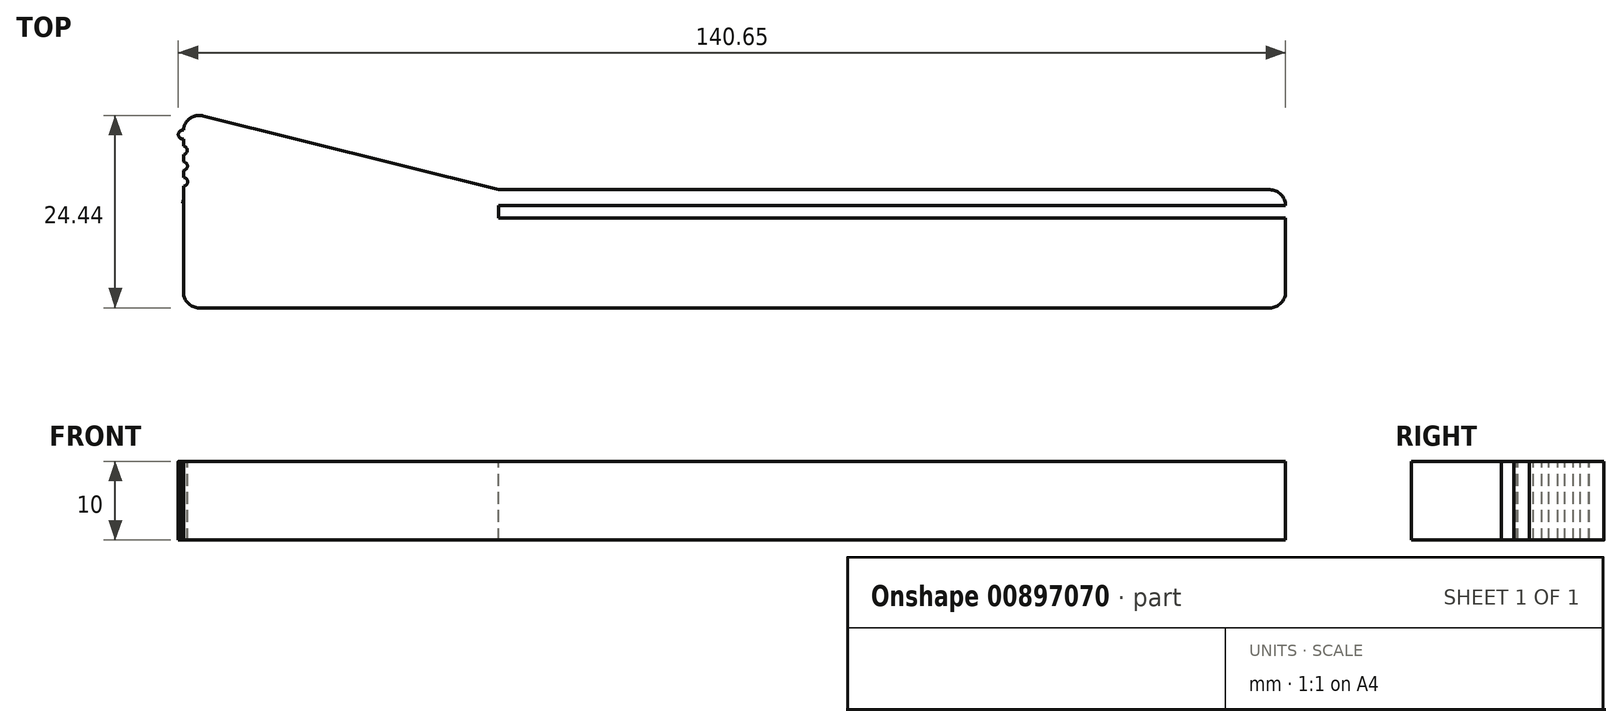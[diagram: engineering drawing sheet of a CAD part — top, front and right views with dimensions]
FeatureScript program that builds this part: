
annotation { "Feature Type Name" : "Feature", "Feature Type Description" : "" }
export const myFeature = defineFeature(function(context is Context, id is Id, definition is map)
    precondition{}
    {
        {
            var Q0;
            Q0=qCreatedBy(makeId("Top.planeOp"),FACE);
            var sketch = newSketch(context, id + "F0", { "sketchPlane" : qUnion([Q0])});
            skLineSegment(sketch, "E0.bottom", {"start": v(0, 7.5) * mm, "end": v(98, 7.5) * mm});
            skLineSegment(sketch, "E0.top", {"start": v(0, -7.5) * mm, "end": v(98, -7.5) * mm});
            skLineSegment(sketch, "E0.left", {"start": v(0, 7.5) * mm, "end": v(0, -7.5) * mm});
            skLineSegment(sketch, "E0.right", {"start": v(100, 5.5) * mm, "end": v(100, -5.5) * mm});
            skLineSegment(sketch, "E1", {"start": v(0, -7.5) * mm, "end": v(-38, -7.5) * mm});
            skLineSegment(sketch, "E2", {"start": v(-40, -5.5) * mm, "end": v(-40, 14.94) * mm});
            skLineSegment(sketch, "E3", {"start": v(-37.51, 16.88) * mm, "end": v(0, 7.5) * mm});
            skPoint(sketch, "E4.visualSharp", {"position": v(-40, 17.5) * mm});
            skArc(sketch, "E4.filletArc", {"start": v(-37.51, 16.88) * mm, "mid": v(-39.23, 16.51) * mm, "end": v(-40, 14.94) * mm});
            skPoint(sketch, "E5.visualSharp", {"position": v(-40, -7.5) * mm});
            skArc(sketch, "E5.filletArc", {"start": v(-40, -5.5) * mm, "mid": v(-39.41, -6.91) * mm, "end": v(-38, -7.5) * mm});
            skPoint(sketch, "E6.visualSharp", {"position": v(100, 7.5) * mm});
            skArc(sketch, "E6.filletArc", {"start": v(100, 5.5) * mm, "mid": v(99.41, 6.91) * mm, "end": v(98, 7.5) * mm});
            skPoint(sketch, "E7.visualSharp", {"position": v(100, -7.5) * mm});
            skArc(sketch, "E7.filletArc", {"start": v(98, -7.5) * mm, "mid": v(99.41, -6.91) * mm, "end": v(100, -5.5) * mm});
            skPoint(sketch, "E8", {"position": v(-14, -1.5) * mm});
            skLineSegment(sketch, "E9.bottom", {"start": v(-18.83, -0.2) * mm, "end": v(-43.6, -0.2) * mm});
            skLineSegment(sketch, "E9.top", {"start": v(-18.83, -2.8) * mm, "end": v(-43.6, -2.8) * mm});
            skLineSegment(sketch, "E9.left", {"start": v(-18.83, -0.2) * mm, "end": v(-18.83, -2.8) * mm});
            skLineSegment(sketch, "E9.right", {"start": v(-43.6, -0.2) * mm, "end": v(-43.6, -2.8) * mm});
            skCircle(sketch, "E10", {"center": v(-14, -1.5) * mm, "radius": 5 * mm});
            skLineSegment(sketch, "E11", {"start": v(-15.93, 3.11) * mm, "end": v(-23.83, -0.2) * mm});
            skLineSegment(sketch, "E12", {"start": v(-15.93, -6.11) * mm, "end": v(-23.83, -2.8) * mm});
            skCircle(sketch, "E13", {"center": v(-14, -1.5) * mm, "radius": 3.4 * mm});
            skLineSegment(sketch, "E14.bottom", {"start": v(100, 5.5) * mm, "end": v(-40, 5.5) * mm});
            skLineSegment(sketch, "E14.top", {"start": v(100, 3.9) * mm, "end": v(-40, 3.9) * mm});
            skLineSegment(sketch, "E14.left", {"start": v(100, 5.5) * mm, "end": v(100, 3.9) * mm});
            skLineSegment(sketch, "E14.right", {"start": v(-40, 5.5) * mm, "end": v(-40, 3.9) * mm});
            skCircle(sketch, "E15", {"center": v(-40, 6.51) * mm, "radius": 0.56 * mm});
            skCircle(sketch, "E16.1.0.0", {"center": v(-40.02, 8.51) * mm, "radius": 0.56 * mm});
            skCircle(sketch, "E16.2.0.0", {"center": v(-40.05, 10.5) * mm, "radius": 0.56 * mm});
            skCircle(sketch, "E16.3.0.0", {"center": v(-40.07, 12.5) * mm, "radius": 0.56 * mm});
            skCircle(sketch, "E16.4.0.0", {"center": v(-40.1, 14.5) * mm, "radius": 0.56 * mm});
            skLineSegment(sketch, "E16.direction1", {"start": v(-40, 6.51) * mm, "end": v(-40.02, 8.51) * mm, "construction": true});
            skLineSegment(sketch, "E17", {"start": v(-40.26, 6.02) * mm, "end": v(-39.23, 5.5) * mm});
            skLineSegment(sketch, "E18", {"start": v(-15.32, 1.64) * mm, "end": v(-22.8, -1.5) * mm});
            skLineSegment(sketch, "E19", {"start": v(-22.8, -1.5) * mm, "end": v(-15.32, -4.64) * mm});
            skSolve(sketch);
        }
        {
            var Q0;
            Q0=makeQuery(id+"F0.imprint","IMPRINT",FACE,{"disambiguationData":[TD([[makeQuery(id+"F0.imprint","IMPRINT",EDGE,{"derivedFrom":sQuery(id+"F0.wireOp",EDGE,"E0.left")}),-1.0]])]});
            var Q1;
            Q1=makeQuery(id+"F0.imprint","IMPRINT",FACE,{"disambiguationData":[TD([[makeQuery(id+"F0.imprint","IMPRINT",EDGE,{"derivedFrom":sQuery(id+"F0.wireOp",EDGE,"E0.bottom")}),-1.0]])]});
            var Q2;
            {var subQ5=sQuery(id+"F0.wireOp",EDGE,"E9.left");Q2=makeQuery(id+"F0.imprint","IMPRINT",FACE,{"disambiguationData":[TD([[makeQuery(id+"F0.imprint","IMPRINT",EDGE,{"derivedFrom":subQ5}),-1.0]])]});}
            var Q3;
            Q3=makeQuery(id+"F0.imprint","IMPRINT",FACE,{"disambiguationData":[TD([[makeQuery(id+"F0.imprint","IMPRINT",EDGE,{"derivedFrom":sQuery(id+"F0.wireOp",EDGE,"E13")}),1.0]])]});
            var Q4;
            {var subQ2=sQuery(id+"F0.wireOp",EDGE,"E2");var subQ7=sQuery(id+"F0.wireOp",EDGE,"E9.top");var subQ10=makeQuery(id+"F0.imprint","INTERSECT",VERTEX,{"derivedFrom":[subQ2,subQ7]});Q4=makeQuery(id+"F0.imprint","IMPRINT",FACE,{"disambiguationData":[TD([[makeQuery(id+"F0.imprint","IMPRINT",EDGE,{"disambiguationData":[TD([[subQ10,-1.0]])],"derivedFrom":subQ2}),-1.0]])]});}
            var Q5;
            {var subQ3=sQuery(id+"F0.wireOp",EDGE,"E12");Q5=makeQuery(id+"F0.imprint","IMPRINT",FACE,{"disambiguationData":[TD([[makeQuery(id+"F0.imprint","IMPRINT",EDGE,{"derivedFrom":subQ3}),-1.0]])]});}
            var Q6;
            {var subQ3=sQuery(id+"F0.wireOp",EDGE,"E11");Q6=makeQuery(id+"F0.imprint","IMPRINT",FACE,{"disambiguationData":[TD([[makeQuery(id+"F0.imprint","IMPRINT",EDGE,{"derivedFrom":subQ3}),1.0]])]});}
            var Q7;
            {var subQ1=sQuery(id+"F0.wireOp",EDGE,"E9.left");Q7=makeQuery(id+"F0.imprint","IMPRINT",FACE,{"disambiguationData":[TD([[makeQuery(id+"F0.imprint","IMPRINT",EDGE,{"derivedFrom":subQ1}),1.0]])]});}
            var Q8;
            {var subQ0=sQuery(id+"F0.wireOp",EDGE,"E3");Q8=makeQuery(id+"F0.imprint","IMPRINT",FACE,{"disambiguationData":[TD([[makeQuery(id+"F0.imprint","IMPRINT",EDGE,{"derivedFrom":subQ0}),-1.0]])]});}
            var Q9;
            {var subQ3=sQuery(id+"F0.wireOp",EDGE,"E1");Q9=makeQuery(id+"F0.imprint","IMPRINT",FACE,{"disambiguationData":[TD([[makeQuery(id+"F0.imprint","IMPRINT",EDGE,{"derivedFrom":subQ3}),-1.0]])]});}
            var Q10;
            {var subQ1=sQuery(id+"F0.wireOp",EDGE,"E0.top");Q10=makeQuery(id+"F0.imprint","IMPRINT",FACE,{"disambiguationData":[TD([[makeQuery(id+"F0.imprint","IMPRINT",EDGE,{"derivedFrom":subQ1}),1.0]])]});}
            var Q11;
            {var subQ5=sQuery(id+"F0.wireOp",EDGE,"E14.left");Q11=makeQuery(id+"F0.imprint","IMPRINT",FACE,{"disambiguationData":[TD([[makeQuery(id+"F0.imprint","IMPRINT",EDGE,{"derivedFrom":subQ5}),-1.0]])]});}
            var Q12;
            {var subQ0=sQuery(id+"F0.wireOp",EDGE,"E15");var subQ1=sQuery(id+"F0.wireOp",EDGE,"E2");var subQ3=makeQuery(id+"F0.imprint","INTERSECT",VERTEX,{"derivedFrom":[subQ1,subQ0]});Q12=makeQuery(id+"F0.imprint","IMPRINT",FACE,{"disambiguationData":[TD([[makeQuery(id+"F0.imprint","IMPRINT",EDGE,{"disambiguationData":[TD([[subQ3,1.0]])],"derivedFrom":subQ1}),1.0]])]});}
            var Q13;
            {var subQ0=sQuery(id+"F0.wireOp",EDGE,"E15");var subQ1=sQuery(id+"F0.wireOp",EDGE,"E2");var subQ3=makeQuery(id+"F0.imprint","INTERSECT",VERTEX,{"derivedFrom":[subQ1,subQ0]});Q13=makeQuery(id+"F0.imprint","IMPRINT",FACE,{"disambiguationData":[TD([[makeQuery(id+"F0.imprint","IMPRINT",EDGE,{"disambiguationData":[TD([[subQ3,1.0]])],"derivedFrom":subQ1}),-1.0]])]});}
            var Q14;
            {var subQ0=sQuery(id+"F0.wireOp",EDGE,"E16.1.0.0");var subQ1=sQuery(id+"F0.wireOp",EDGE,"E2");var subQ2=makeQuery(id+"F0.imprint","INTERSECT",VERTEX,{"disambiguationData":[OD(0.0)],"derivedFrom":[subQ1,subQ0]});Q14=makeQuery(id+"F0.imprint","IMPRINT",FACE,{"disambiguationData":[TD([[makeQuery(id+"F0.imprint","IMPRINT",EDGE,{"disambiguationData":[TD([[subQ2,-1.0]])],"derivedFrom":subQ1}),1.0]])]});}
            var Q15;
            {var subQ0=sQuery(id+"F0.wireOp",EDGE,"E16.1.0.0");var subQ1=sQuery(id+"F0.wireOp",EDGE,"E2");var subQ2=makeQuery(id+"F0.imprint","INTERSECT",VERTEX,{"disambiguationData":[OD(0.0)],"derivedFrom":[subQ1,subQ0]});Q15=makeQuery(id+"F0.imprint","IMPRINT",FACE,{"disambiguationData":[TD([[makeQuery(id+"F0.imprint","IMPRINT",EDGE,{"disambiguationData":[TD([[subQ2,-1.0]])],"derivedFrom":subQ1}),-1.0]])]});}
            var Q16;
            {var subQ0=sQuery(id+"F0.wireOp",EDGE,"E16.2.0.0");var subQ1=sQuery(id+"F0.wireOp",EDGE,"E2");var subQ2=makeQuery(id+"F0.imprint","INTERSECT",VERTEX,{"disambiguationData":[OD(0.0)],"derivedFrom":[subQ1,subQ0]});Q16=makeQuery(id+"F0.imprint","IMPRINT",FACE,{"disambiguationData":[TD([[makeQuery(id+"F0.imprint","IMPRINT",EDGE,{"disambiguationData":[TD([[subQ2,-1.0]])],"derivedFrom":subQ1}),1.0]])]});}
            var Q17;
            {var subQ0=sQuery(id+"F0.wireOp",EDGE,"E16.3.0.0");var subQ1=sQuery(id+"F0.wireOp",EDGE,"E2");var subQ2=makeQuery(id+"F0.imprint","INTERSECT",VERTEX,{"disambiguationData":[OD(0.0)],"derivedFrom":[subQ1,subQ0]});Q17=makeQuery(id+"F0.imprint","IMPRINT",FACE,{"disambiguationData":[TD([[makeQuery(id+"F0.imprint","IMPRINT",EDGE,{"disambiguationData":[TD([[subQ2,-1.0]])],"derivedFrom":subQ1}),1.0]])]});}
            var Q18;
            {var subQ0=sQuery(id+"F0.wireOp",EDGE,"E4.filletArc");var subQ1=sQuery(id+"F0.wireOp",EDGE,"E2");var subQ2=makeQuery(id+"F0.imprint","INTERSECT",VERTEX,{"derivedFrom":[subQ1,subQ0]});Q18=makeQuery(id+"F0.imprint","IMPRINT",FACE,{"disambiguationData":[TD([[makeQuery(id+"F0.imprint","IMPRINT",EDGE,{"disambiguationData":[TD([[subQ2,1.0]])],"derivedFrom":subQ1}),1.0]])]});}
            var Q19;
            {var subQ0=sQuery(id+"F0.wireOp",EDGE,"E4.filletArc");var subQ1=sQuery(id+"F0.wireOp",EDGE,"E2");var subQ2=makeQuery(id+"F0.imprint","INTERSECT",VERTEX,{"derivedFrom":[subQ1,subQ0]});Q19=makeQuery(id+"F0.imprint","IMPRINT",FACE,{"disambiguationData":[TD([[makeQuery(id+"F0.imprint","IMPRINT",EDGE,{"disambiguationData":[TD([[subQ2,1.0]])],"derivedFrom":subQ1}),-1.0]])]});}
            var Q20;
            {var subQ0=sQuery(id+"F0.wireOp",EDGE,"E16.3.0.0");var subQ1=sQuery(id+"F0.wireOp",EDGE,"E2");var subQ2=makeQuery(id+"F0.imprint","INTERSECT",VERTEX,{"disambiguationData":[OD(0.0)],"derivedFrom":[subQ1,subQ0]});Q20=makeQuery(id+"F0.imprint","IMPRINT",FACE,{"disambiguationData":[TD([[makeQuery(id+"F0.imprint","IMPRINT",EDGE,{"disambiguationData":[TD([[subQ2,-1.0]])],"derivedFrom":subQ1}),-1.0]])]});}
            var Q21;
            {var subQ0=sQuery(id+"F0.wireOp",EDGE,"E16.2.0.0");var subQ1=sQuery(id+"F0.wireOp",EDGE,"E2");var subQ2=makeQuery(id+"F0.imprint","INTERSECT",VERTEX,{"disambiguationData":[OD(0.0)],"derivedFrom":[subQ1,subQ0]});Q21=makeQuery(id+"F0.imprint","IMPRINT",FACE,{"disambiguationData":[TD([[makeQuery(id+"F0.imprint","IMPRINT",EDGE,{"disambiguationData":[TD([[subQ2,-1.0]])],"derivedFrom":subQ1}),-1.0]])]});}
            var Q22;
            {var subQ0=sQuery(id+"F0.wireOp",EDGE,"E14.bottom");var subQ3=sQuery(id+"F0.wireOp",EDGE,"E17");var subQ5=makeQuery(id+"F0.imprint","INTERSECT",VERTEX,{"derivedFrom":[subQ0,subQ3]});Q22=makeQuery(id+"F0.imprint","IMPRINT",FACE,{"disambiguationData":[TD([[makeQuery(id+"F0.imprint","IMPRINT",EDGE,{"disambiguationData":[TD([[subQ5,1.0]])],"derivedFrom":subQ3}),-1.0]])]});}
            var Q23;
            {var subQ0=sQuery(id+"F0.wireOp",EDGE,"E19");var subQ1=sQuery(id+"F0.wireOp",EDGE,"E18");var subQ2=makeQuery(id+"F0.imprint","INTERSECT",VERTEX,{"derivedFrom":[subQ1,subQ0]});Q23=makeQuery(id+"F0.imprint","IMPRINT",FACE,{"disambiguationData":[TD([[makeQuery(id+"F0.imprint","IMPRINT",EDGE,{"disambiguationData":[TD([[subQ2,1.0]])],"derivedFrom":subQ1}),1.0]])]});}
            var Q24;
            {var subQ1=sQuery(id+"F0.wireOp",EDGE,"E9.top");var subQ3=sQuery(id+"F0.wireOp",EDGE,"E19");var subQ4=makeQuery(id+"F0.imprint","INTERSECT",VERTEX,{"derivedFrom":[subQ1,subQ3]});Q24=makeQuery(id+"F0.imprint","IMPRINT",FACE,{"disambiguationData":[TD([[makeQuery(id+"F0.imprint","IMPRINT",EDGE,{"disambiguationData":[TD([[subQ4,-1.0]])],"derivedFrom":subQ3}),1.0]])]});}
            var Q25;
            {var subQ1=sQuery(id+"F0.wireOp",EDGE,"E9.bottom");var subQ3=sQuery(id+"F0.wireOp",EDGE,"E18");var subQ4=makeQuery(id+"F0.imprint","INTERSECT",VERTEX,{"derivedFrom":[subQ1,subQ3]});Q25=makeQuery(id+"F0.imprint","IMPRINT",FACE,{"disambiguationData":[TD([[makeQuery(id+"F0.imprint","IMPRINT",EDGE,{"disambiguationData":[TD([[subQ4,1.0]])],"derivedFrom":subQ3}),1.0]])]});}
            var Q26;
            {var subQ5=sQuery(id+"F0.wireOp",EDGE,"E10");var subQ8=makeQuery(id+"F0.imprint","INTERSECT",VERTEX,{"derivedFrom":[subQ5,sQuery(id+"F0.wireOp",EDGE,"E11")]});Q26=makeQuery(id+"F0.imprint","IMPRINT",FACE,{"disambiguationData":[TD([[makeQuery(id+"F0.imprint","IMPRINT",EDGE,{"disambiguationData":[TD([[subQ8,-1.0]])],"derivedFrom":subQ5}),1.0]])]});}
            extrude(context, id + "F1", {"entities" : qUnion([Q0, Q1, Q2, Q3, Q4, Q5, Q6, Q7, Q8, Q9, Q10, Q11, Q12, Q13, Q14, Q15, Q16, Q17, Q18, Q19, Q20, Q21, Q22, Q23, Q24, Q25, Q26]), "oppositeDirection" : true, "depth" : 10 * mm, "offsetDistance" : 25 * mm});
        }
    });
